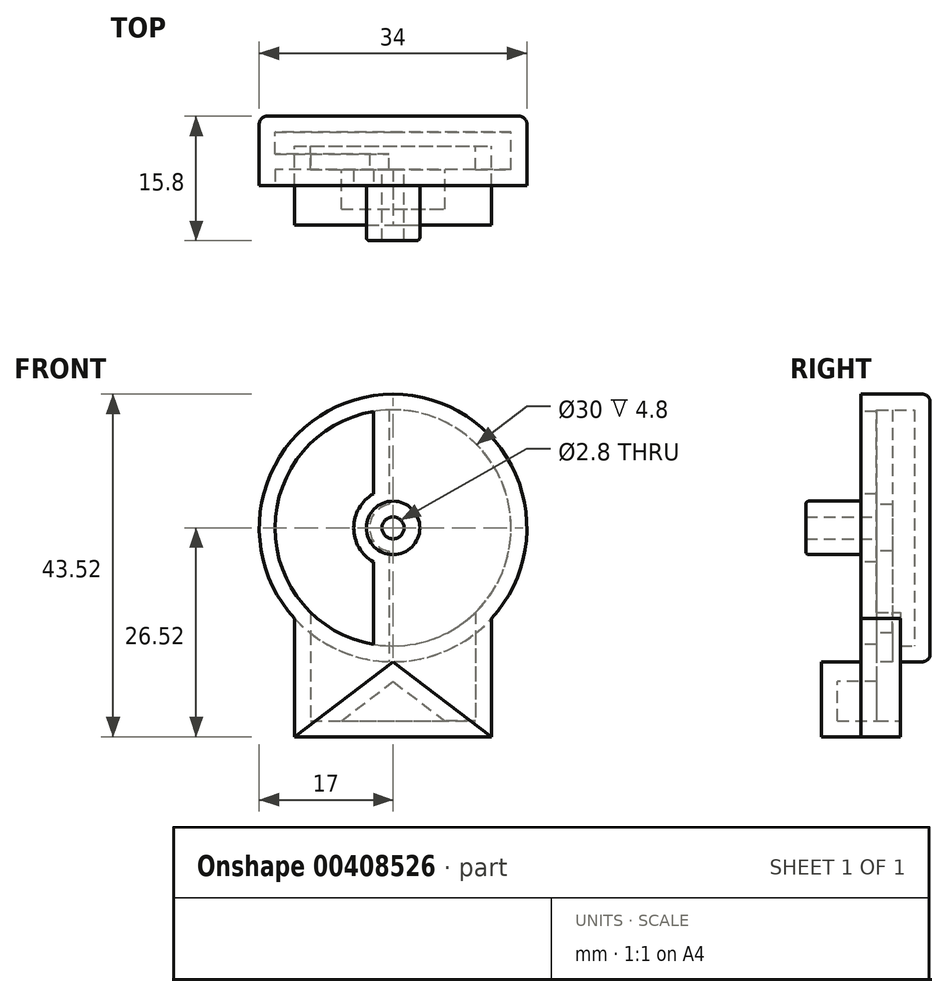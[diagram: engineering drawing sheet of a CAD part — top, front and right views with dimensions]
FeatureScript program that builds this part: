
annotation { "Feature Type Name" : "Feature", "Feature Type Description" : "" }
export const myFeature = defineFeature(function(context is Context, id is Id, definition is map)
    precondition{}
    {
        {
            var Q0;
            Q0=qCreatedBy(makeId("Front.planeOp"),FACE);
            var sketch = newSketch(context, id + "F0", { "sketchPlane" : qUnion([Q0])});
            skCircle(sketch, "E0", {"center": v(0, 0) * mm, "radius": 17 * mm});
            skLineSegment(sketch, "E1.bottom", {"start": v(-12.5, -11.52) * mm, "end": v(12.5, -11.52) * mm, "construction": true});
            skLineSegment(sketch, "E1.top", {"start": v(-12.5, -26.52) * mm, "end": v(12.5, -26.52) * mm});
            skLineSegment(sketch, "E1.left", {"start": v(-12.5, -11.52) * mm, "end": v(-12.5, -26.52) * mm});
            skLineSegment(sketch, "E1.right", {"start": v(12.5, -11.52) * mm, "end": v(12.5, -26.52) * mm});
            skLineSegment(sketch, "E2", {"start": v(0, 0) * mm, "end": v(0, -26.52) * mm, "construction": true});
            skPoint(sketch, "E3", {"position": v(0, -26.52) * mm});
            skSolve(sketch);
        }
        {
            var Q0;
            Q0=qSketchRegion(id+"F0",true);
            extrude(context, id + "F1", {"entities" : qUnion([Q0]), "depth" : 10 * mm});
        }
        {
            var Q0;
            Q0=makeQuery(id+"F1.opExtrude","CAP_FACE",FACE,{"disambiguationData":[OSD([sQuery(id+"F0.wireOp",EDGE,"E0"),sQuery(id+"F0.wireOp",EDGE,"E1.top"),sQuery(id+"F0.wireOp",EDGE,"E1.left"),sQuery(id+"F0.wireOp",EDGE,"E1.right")])],"isStart":false});
            var sketch = newSketch(context, id + "F2", { "sketchPlane" : qUnion([Q0])});
            skCircle(sketch, "E4", {"center": v(0, 0) * mm, "radius": 17 * mm});
            skSolve(sketch);
        }
        {
            var Q0;
            Q0 = qSketchRegion(id + "F2", true);
            extrude(context, id + "F3", {"entities" : qUnion([Q0]), "operationType" : NewBodyOperationType.REMOVE, "oppositeDirection" : true, "depth" : 5 * mm});
        }
        {
            var Q0;
            Q0=makeQuery(id+"F1.opExtrude","CAP_FACE",FACE,{"disambiguationData":[OSD([sQuery(id+"F0.wireOp",EDGE,"E0"),sQuery(id+"F0.wireOp",EDGE,"E1.top"),sQuery(id+"F0.wireOp",EDGE,"E1.left"),sQuery(id+"F0.wireOp",EDGE,"E1.right")])],"isStart":true});
            var sketch = newSketch(context, id + "F4", { "sketchPlane" : qUnion([Q0])});
            skCircle(sketch, "E5", {"center": v(0, 0) * mm, "radius": 17 * mm});
            skSolve(sketch);
        }
        {
            var Q0;
            Q0 = qSketchRegion(id + "F4", true);
            extrude(context, id + "F5", {"entities" : qUnion([Q0]), "operationType" : NewBodyOperationType.ADD, "depth" : 3.8 * mm});
        }
        {
            var Q0;
            Q0=makeQuery(id+"F5.opExtrude","CAP_EDGE",EDGE,{"disambiguationData":[OSD([sQuery(id+"F4.wireOp",EDGE,"E5")])],"isStart":false});
            fillet(context, id + "F6", {"entities" : qUnion([Q0]), "radius" : 1 * mm, "tangentPropagation" : true, "allowEdgeOverflow" : false});
        }
        {
            var Q0;
            Q0=makeQuery(id+"F3.boolean.opBoolean","COPY",FACE,{"derivedFrom":makeQuery(id+"F3.opExtrude","CAP_FACE",FACE,{"disambiguationData":[OSD([sQuery(id+"F2.wireOp",EDGE,"E4")])],"isStart":false})});
            var sketch = newSketch(context, id + "F7", { "sketchPlane" : qUnion([Q0])});
            skCircle(sketch, "E6", {"center": v(0, 0) * mm, "radius": 15 * mm, "construction": true});
            skCircle(sketch, "E7", {"center": v(0, 0) * mm, "radius": 5 * mm, "construction": true});
            skLineSegment(sketch, "E8", {"start": v(0, 15) * mm, "end": v(0, -15) * mm, "construction": true});
            skArc(sketch, "E9", {"start": v(-2.5, 14.8) * mm, "mid": v(-15, 0) * mm, "end": v(-2.5, -14.8) * mm});
            skArc(sketch, "E10", {"start": v(-2.5, 4.33) * mm, "mid": v(-5, 0) * mm, "end": v(-2.5, -4.33) * mm});
            skLineSegment(sketch, "E11", {"start": v(-2.5, 14.8) * mm, "end": v(-2.5, -14.8) * mm, "construction": true});
            skLineSegment(sketch, "E12", {"start": v(-2.5, -4.33) * mm, "end": v(-2.5, -14.8) * mm});
            skLineSegment(sketch, "E13", {"start": v(-2.5, 14.8) * mm, "end": v(-2.5, 4.33) * mm});
            skSolve(sketch);
        }
        {
            var Q0;
            Q0=qSketchRegion(id+"F7",true);
            extrude(context, id + "F8", {"entities" : qUnion([Q0]), "operationType" : NewBodyOperationType.REMOVE, "oppositeDirection" : true, "depth" : 2 * mm});
        }
        {
            var Q0;
            Q0=makeQuery(id+"F3.boolean.opBoolean","COPY",FACE,{"derivedFrom":makeQuery(id+"F3.opExtrude","CAP_FACE",FACE,{"disambiguationData":[OSD([sQuery(id+"F2.wireOp",EDGE,"E4")])],"isStart":false})});
            var sketch = newSketch(context, id + "F9", { "sketchPlane" : qUnion([Q0])});
            skCircle(sketch, "E14", {"center": v(0, 0) * mm, "radius": 3.4 * mm});
            skSolve(sketch);
        }
        {
            var Q0;
            Q0=qSketchRegion(id+"F9",true);
            extrude(context, id + "F10", {"entities" : qUnion([Q0]), "operationType" : NewBodyOperationType.ADD, "depth" : 7 * mm});
        }
        {
            var Q0;
            Q0=makeQuery(id+"F1.opExtrude","CAP_FACE",FACE,{"disambiguationData":[OSD([sQuery(id+"F0.wireOp",EDGE,"E0"),sQuery(id+"F0.wireOp",EDGE,"E1.top"),sQuery(id+"F0.wireOp",EDGE,"E1.left"),sQuery(id+"F0.wireOp",EDGE,"E1.right")])],"isStart":false});
            var sketch = newSketch(context, id + "F11", { "sketchPlane" : qUnion([Q0])});
            skLineSegment(sketch, "E15", {"start": v(-12.5, -26.52) * mm, "end": v(0, -17) * mm});
            skLineSegment(sketch, "E16", {"start": v(0, -17) * mm, "end": v(12.5, -26.52) * mm});
            skLineSegment(sketch, "E17", {"start": v(12.5, -26.52) * mm, "end": v(12.5, -11.52) * mm});
            skLineSegment(sketch, "E18", {"start": v(-12.5, -26.52) * mm, "end": v(-12.5, -11.52) * mm});
            skArc(sketch, "E19.0", {"start": v(-12.5, -11.52) * mm, "mid": v(0, -17) * mm, "end": v(12.5, -11.52) * mm});
            skSolve(sketch);
        }
        {
            var Q0;
            Q0 = qSketchRegion(id + "F11", true);
            extrude(context, id + "F12", {"entities" : qUnion([Q0]), "operationType" : NewBodyOperationType.REMOVE, "oppositeDirection" : true, "depth" : 5 * mm});
        }
        {
            var Q0;
            Q0=makeQuery(id+"F1.opExtrude","CAP_FACE",FACE,{"disambiguationData":[OSD([sQuery(id+"F0.wireOp",EDGE,"E0"),sQuery(id+"F0.wireOp",EDGE,"E1.top"),sQuery(id+"F0.wireOp",EDGE,"E1.left"),sQuery(id+"F0.wireOp",EDGE,"E1.right")])],"isStart":true});
            shell(context, id + "F13", {"entities" : qUnion([Q0]), "thickness" : 2 * mm});
        }
        {
            var Q0;
            Q0=makeQuery(id+"F10.opExtrude","CAP_EDGE",EDGE,{"disambiguationData":[OSD([sQuery(id+"F9.wireOp",EDGE,"E14")])],"isStart":true});
            var Q1;
            Q1=makeQuery(id+"F10.opExtrude","CAP_EDGE",EDGE,{"disambiguationData":[OSD([sQuery(id+"F9.wireOp",EDGE,"E14")])],"isStart":false});
            fillet(context, id + "F14", {"entities" : qUnion([Q0, Q1]), "radius" : .4 * mm, "tangentPropagation" : true, "allowEdgeOverflow" : false});
        }
        {
            var Q0;
            {var subQ0=sQuery(id+"F9.wireOp",EDGE,"E14");Q0=makeQuery(id+"F13.opShell","OFFSET_FACE",FACE,{"disambiguationData":[OSD([subQ0]),TDD([makeQuery(id+"F10.opExtrude","CAP_FACE",FACE,{"disambiguationData":[OSD([subQ0])],"isStart":false})])]});}
            extrude(context, id + "F16", {"entities" : qUnion([Q0]), "operationType" : NewBodyOperationType.REMOVE, "oppositeDirection" : true, "depth" : 25 * mm});
        }
    });
